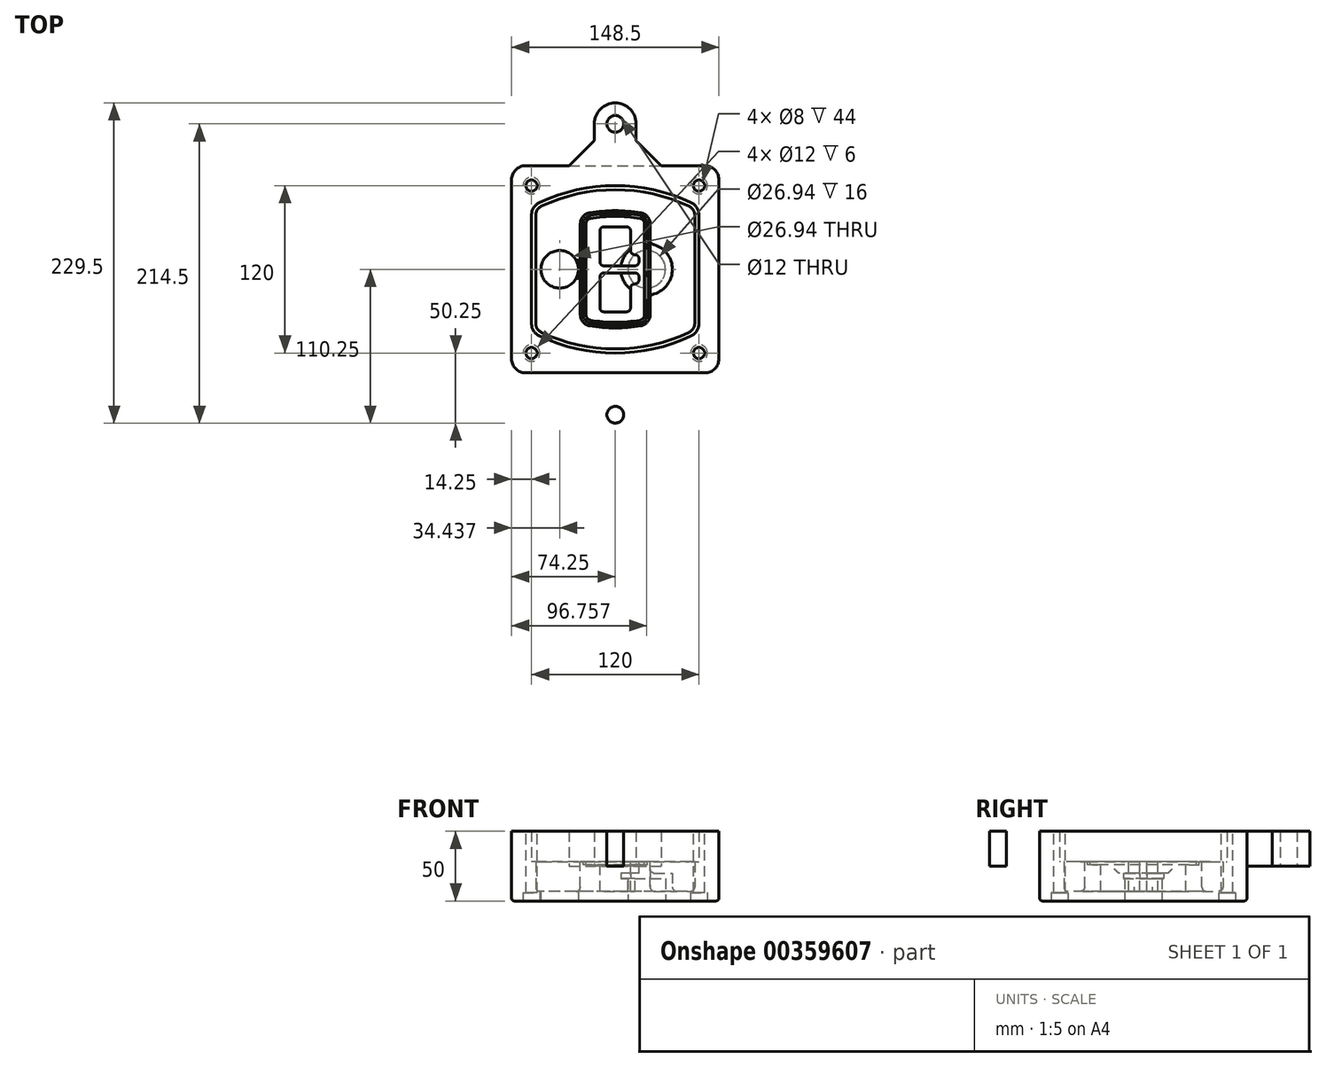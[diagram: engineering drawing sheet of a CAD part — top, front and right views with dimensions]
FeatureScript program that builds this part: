
annotation { "Feature Type Name" : "Feature", "Feature Type Description" : "" }
export const myFeature = defineFeature(function(context is Context, id is Id, definition is map)
    precondition{}
    {
        {
            var Q0;
            Q0=qCreatedBy(makeId("Top.planeOp"),FACE);
            var sketch = newSketch(context, id + "F0", { "sketchPlane" : qUnion([Q0])});
            skPoint(sketch, "E0.rect.middle", {"position": v(0, 0) * mm});
            skLineSegment(sketch, "E1.bottom", {"start": v(-64.25, -74.25) * mm, "end": v(64.25, -74.25) * mm});
            skLineSegment(sketch, "E1.top", {"start": v(-64.25, 74.25) * mm, "end": v(64.25, 74.25) * mm});
            skLineSegment(sketch, "E1.left", {"start": v(-74.25, -64.25) * mm, "end": v(-74.25, 64.25) * mm});
            skLineSegment(sketch, "E1.right", {"start": v(74.25, -64.25) * mm, "end": v(74.25, 64.25) * mm});
            skLineSegment(sketch, "E2", {"start": v(-74.25, 74.25) * mm, "end": v(74.25, -74.25) * mm, "construction": true});
            skLineSegment(sketch, "E3", {"start": v(74.25, 74.25) * mm, "end": v(-74.25, -74.25) * mm, "construction": true});
            skCircle(sketch, "E4", {"center": v(-60, 60) * mm, "radius": 4 * mm});
            skCircle(sketch, "E5", {"center": v(60, 60) * mm, "radius": 4 * mm});
            skCircle(sketch, "E6", {"center": v(60, -60) * mm, "radius": 4 * mm});
            skCircle(sketch, "E7", {"center": v(-60, -60) * mm, "radius": 4 * mm});
            skLineSegment(sketch, "E8", {"start": v(-60, 60) * mm, "end": v(60, 60) * mm, "construction": true});
            skLineSegment(sketch, "E9", {"start": v(60, 60) * mm, "end": v(60, -60) * mm, "construction": true});
            skLineSegment(sketch, "E10", {"start": v(60, -60) * mm, "end": v(-60, -60) * mm, "construction": true});
            skLineSegment(sketch, "E11", {"start": v(-60, -60) * mm, "end": v(-60, 60) * mm, "construction": true});
            skLineSegment(sketch, "E12", {"start": v(-60, 38.83) * mm, "end": v(-60, -38.83) * mm});
            skLineSegment(sketch, "E13", {"start": v(60, 38.83) * mm, "end": v(60, -38.83) * mm});
            skArc(sketch, "E14", {"start": v(54.26, 47.88) * mm, "mid": v(0, 60) * mm, "end": v(-54.26, 47.88) * mm});
            skArc(sketch, "E15", {"start": v(-54.26, -47.88) * mm, "mid": v(0, -60) * mm, "end": v(54.26, -47.88) * mm});
            skLineSegment(sketch, "E16", {"start": v(-60, 0) * mm, "end": v(60, 0) * mm, "construction": true});
            skPoint(sketch, "E17.visualSharp", {"position": v(-60, -45) * mm});
            skArc(sketch, "E17.filletArc", {"start": v(-60, -38.83) * mm, "mid": v(-58.44, -44.2) * mm, "end": v(-54.26, -47.88) * mm});
            skPoint(sketch, "E18.visualSharp", {"position": v(-60, 45) * mm});
            skArc(sketch, "E18.filletArc", {"start": v(-54.26, 47.88) * mm, "mid": v(-58.44, 44.2) * mm, "end": v(-60, 38.83) * mm});
            skPoint(sketch, "E19.visualSharp", {"position": v(60, 45) * mm});
            skArc(sketch, "E19.filletArc", {"start": v(60, 38.83) * mm, "mid": v(58.44, 44.2) * mm, "end": v(54.26, 47.88) * mm});
            skPoint(sketch, "E20.visualSharp", {"position": v(60, -45) * mm});
            skArc(sketch, "E20.filletArc", {"start": v(54.26, -47.88) * mm, "mid": v(58.44, -44.2) * mm, "end": v(60, -38.83) * mm});
            skPoint(sketch, "E21.visualSharp", {"position": v(-74.25, 74.25) * mm});
            skArc(sketch, "E21.filletArc", {"start": v(-64.25, 74.25) * mm, "mid": v(-71.32, 71.32) * mm, "end": v(-74.25, 64.25) * mm});
            skPoint(sketch, "E22.visualSharp", {"position": v(74.25, 74.25) * mm});
            skArc(sketch, "E22.filletArc", {"start": v(74.25, 64.25) * mm, "mid": v(71.32, 71.32) * mm, "end": v(64.25, 74.25) * mm});
            skPoint(sketch, "E23.visualSharp", {"position": v(74.25, -74.25) * mm});
            skArc(sketch, "E23.filletArc", {"start": v(64.25, -74.25) * mm, "mid": v(71.32, -71.32) * mm, "end": v(74.25, -64.25) * mm});
            skPoint(sketch, "E24.visualSharp", {"position": v(-74.25, -74.25) * mm});
            skArc(sketch, "E24.filletArc", {"start": v(-74.25, -64.25) * mm, "mid": v(-71.32, -71.32) * mm, "end": v(-64.25, -74.25) * mm});
            skArc(sketch, "E25.0", {"start": v(57, 38.83) * mm, "mid": v(55.9, 42.58) * mm, "end": v(52.98, 45.17) * mm});
            skLineSegment(sketch, "E25.1", {"start": v(57, 38.83) * mm, "end": v(57, -38.83) * mm});
            skArc(sketch, "E25.2", {"start": v(52.98, -45.17) * mm, "mid": v(55.9, -42.58) * mm, "end": v(57, -38.83) * mm});
            skArc(sketch, "E25.3", {"start": v(-52.98, -45.17) * mm, "mid": v(0, -57) * mm, "end": v(52.98, -45.17) * mm});
            skArc(sketch, "E25.4", {"start": v(-57, -38.83) * mm, "mid": v(-55.9, -42.58) * mm, "end": v(-52.98, -45.17) * mm});
            skArc(sketch, "E25.5", {"start": v(52.98, 45.17) * mm, "mid": v(0, 57) * mm, "end": v(-52.98, 45.17) * mm});
            skLineSegment(sketch, "E25.6", {"start": v(-57, 38.83) * mm, "end": v(-57, -38.83) * mm});
            skArc(sketch, "E25.7", {"start": v(-52.98, 45.17) * mm, "mid": v(-55.9, 42.58) * mm, "end": v(-57, 38.83) * mm});
            skArc(sketch, "E26.0", {"start": v(-55.96, 51.5) * mm, "mid": v(-61.82, 46.33) * mm, "end": v(-64, 38.83) * mm});
            skArc(sketch, "E26.1", {"start": v(55.96, 51.5) * mm, "mid": v(0, 64) * mm, "end": v(-55.96, 51.5) * mm});
            skArc(sketch, "E26.2", {"start": v(64, 38.83) * mm, "mid": v(61.82, 46.33) * mm, "end": v(55.96, 51.5) * mm});
            skLineSegment(sketch, "E26.3", {"start": v(64, 38.83) * mm, "end": v(64, -38.83) * mm});
            skArc(sketch, "E26.4", {"start": v(55.96, -51.5) * mm, "mid": v(61.82, -46.33) * mm, "end": v(64, -38.83) * mm});
            skLineSegment(sketch, "E26.5", {"start": v(-64, 38.83) * mm, "end": v(-64, -38.83) * mm});
            skArc(sketch, "E26.6", {"start": v(-55.96, -51.5) * mm, "mid": v(0, -64) * mm, "end": v(55.96, -51.5) * mm});
            skArc(sketch, "E26.7", {"start": v(-64, -38.83) * mm, "mid": v(-61.82, -46.33) * mm, "end": v(-55.96, -51.5) * mm});
            skSolve(sketch);
        }
        {
            var Q0;
            Q0=makeQuery(id+"F0.imprint","IMPRINT",FACE,{"disambiguationData":[TD([[makeQuery(id+"F0.imprint","IMPRINT",EDGE,{"derivedFrom":sQuery(id+"F0.wireOp",EDGE,"E1.bottom")}),1.0]])]});
            var Q1;
            Q1=makeQuery(id+"F0.imprint","IMPRINT",FACE,{"disambiguationData":[TD([[makeQuery(id+"F0.imprint","IMPRINT",EDGE,{"derivedFrom":sQuery(id+"F0.wireOp",EDGE,"E12")}),1.0]])]});
            var Q2;
            Q2=makeQuery(id+"F0.imprint","IMPRINT",FACE,{"disambiguationData":[TD([[makeQuery(id+"F0.imprint","IMPRINT",EDGE,{"derivedFrom":sQuery(id+"F0.wireOp",EDGE,"E25.0")}),1.0]])]});
            var Q3;
            Q3=makeQuery(id+"F0.imprint","IMPRINT",FACE,{"disambiguationData":[TD([[makeQuery(id+"F0.imprint","IMPRINT",EDGE,{"derivedFrom":sQuery(id+"F0.wireOp",EDGE,"E12")}),-1.0]])]});
            extrude(context, id + "F1", {"entities" : qUnion([Q0, Q1, Q2, Q3]), "oppositeDirection" : true, "depth" : 25 * mm});
        }
        {
            var Q0;
            Q0=makeQuery(id+"F0.imprint","IMPRINT",FACE,{"disambiguationData":[TD([[makeQuery(id+"F0.imprint","IMPRINT",EDGE,{"derivedFrom":sQuery(id+"F0.wireOp",EDGE,"E12")}),1.0]])]});
            extrude(context, id + "F2", {"entities" : qUnion([Q0]), "operationType" : NewBodyOperationType.ADD, "depth" : 3 * mm});
        }
        {
            var Q0;
            Q0=makeQuery(id+"F0.imprint","IMPRINT",FACE,{"disambiguationData":[TD([[makeQuery(id+"F0.imprint","IMPRINT",EDGE,{"derivedFrom":sQuery(id+"F0.wireOp",EDGE,"E25.0")}),1.0]])]});
            extrude(context, id + "F3", {"entities" : qUnion([Q0]), "operationType" : NewBodyOperationType.REMOVE, "oppositeDirection" : true, "depth" : 18 * mm});
        }
        {
            var Q0;
            Q0=makeQuery(id+"F2.opExtrude","CAP_FACE",FACE,{"disambiguationData":[OSD([sQuery(id+"F0.wireOp",EDGE,"E12"),sQuery(id+"F0.wireOp",EDGE,"E13"),sQuery(id+"F0.wireOp",EDGE,"E14"),sQuery(id+"F0.wireOp",EDGE,"E15"),sQuery(id+"F0.wireOp",EDGE,"E17.filletArc"),sQuery(id+"F0.wireOp",EDGE,"E18.filletArc"),sQuery(id+"F0.wireOp",EDGE,"E19.filletArc"),sQuery(id+"F0.wireOp",EDGE,"E20.filletArc"),sQuery(id+"F0.wireOp",EDGE,"E25.0"),sQuery(id+"F0.wireOp",EDGE,"E25.1"),sQuery(id+"F0.wireOp",EDGE,"E25.2"),sQuery(id+"F0.wireOp",EDGE,"E25.3"),sQuery(id+"F0.wireOp",EDGE,"E25.4"),sQuery(id+"F0.wireOp",EDGE,"E25.5"),sQuery(id+"F0.wireOp",EDGE,"E25.6"),sQuery(id+"F0.wireOp",EDGE,"E25.7")])],"isStart":false});
            var sketch = newSketch(context, id + "F4", { "sketchPlane" : qUnion([Q0])});
            skArc(sketch, "E27.0", {"start": v(-18.34, -40.45) * mm, "mid": v(0, -42) * mm, "end": v(18.34, -40.45) * mm});
            skArc(sketch, "E28.0", {"start": v(18.34, 40.45) * mm, "mid": v(0, 42) * mm, "end": v(-18.34, 40.45) * mm});
            skLineSegment(sketch, "E29", {"start": v(-25, 32.57) * mm, "end": v(-25, -32.57) * mm});
            skLineSegment(sketch, "E30", {"start": v(25, 32.57) * mm, "end": v(25, -32.57) * mm});
            skLineSegment(sketch, "E31", {"start": v(-25, 39.1) * mm, "end": v(25, 39.1) * mm, "construction": true});
            skLineSegment(sketch, "E32", {"start": v(-25, -39.1) * mm, "end": v(25, -39.1) * mm, "construction": true});
            skPoint(sketch, "E33.visualSharp", {"position": v(-25, 39.1) * mm});
            skArc(sketch, "E33.filletArc", {"start": v(-18.34, 40.45) * mm, "mid": v(-23.11, 37.73) * mm, "end": v(-25, 32.57) * mm});
            skPoint(sketch, "E34.visualSharp", {"position": v(25, 39.1) * mm});
            skArc(sketch, "E34.filletArc", {"start": v(25, 32.57) * mm, "mid": v(23.11, 37.73) * mm, "end": v(18.34, 40.45) * mm});
            skPoint(sketch, "E35.visualSharp", {"position": v(25, -39.1) * mm});
            skArc(sketch, "E35.filletArc", {"start": v(18.34, -40.45) * mm, "mid": v(23.11, -37.73) * mm, "end": v(25, -32.57) * mm});
            skPoint(sketch, "E36.visualSharp", {"position": v(-25, -39.1) * mm});
            skArc(sketch, "E36.filletArc", {"start": v(-25, -32.57) * mm, "mid": v(-23.11, -37.73) * mm, "end": v(-18.34, -40.45) * mm});
            skArc(sketch, "E37.0", {"start": v(52.98, 45.17) * mm, "mid": v(0, 57) * mm, "end": v(-52.98, 45.17) * mm});
            skArc(sketch, "E37.1", {"start": v(-52.98, 45.17) * mm, "mid": v(-55.9, 42.58) * mm, "end": v(-57, 38.83) * mm});
            skLineSegment(sketch, "E37.2", {"start": v(-57, 38.83) * mm, "end": v(-57, -38.83) * mm});
            skArc(sketch, "E37.3", {"start": v(-57, -38.83) * mm, "mid": v(-55.9, -42.58) * mm, "end": v(-52.98, -45.17) * mm});
            skArc(sketch, "E37.4", {"start": v(-52.98, -45.17) * mm, "mid": v(0, -57) * mm, "end": v(52.98, -45.17) * mm});
            skArc(sketch, "E37.5", {"start": v(52.98, -45.17) * mm, "mid": v(55.9, -42.58) * mm, "end": v(57, -38.83) * mm});
            skLineSegment(sketch, "E37.6", {"start": v(57, 38.83) * mm, "end": v(57, -38.83) * mm});
            skArc(sketch, "E37.7", {"start": v(57, 38.83) * mm, "mid": v(55.9, 42.58) * mm, "end": v(52.98, 45.17) * mm});
            skLineSegment(sketch, "E38.0", {"start": v(23, 32.57) * mm, "end": v(23, -32.57) * mm});
            skArc(sketch, "E38.1", {"start": v(18, -38.48) * mm, "mid": v(21.58, -36.44) * mm, "end": v(23, -32.57) * mm});
            skArc(sketch, "E38.2", {"start": v(-18, -38.48) * mm, "mid": v(0, -40) * mm, "end": v(18, -38.48) * mm});
            skArc(sketch, "E38.3", {"start": v(-23, -32.57) * mm, "mid": v(-21.58, -36.44) * mm, "end": v(-18, -38.48) * mm});
            skLineSegment(sketch, "E38.4", {"start": v(-23, 32.57) * mm, "end": v(-23, -32.57) * mm});
            skArc(sketch, "E38.5", {"start": v(23, 32.57) * mm, "mid": v(21.58, 36.44) * mm, "end": v(18, 38.48) * mm});
            skArc(sketch, "E38.6", {"start": v(-18, 38.48) * mm, "mid": v(-21.58, 36.44) * mm, "end": v(-23, 32.57) * mm});
            skArc(sketch, "E38.7", {"start": v(18, 38.48) * mm, "mid": v(0, 40) * mm, "end": v(-18, 38.48) * mm});
            skArc(sketch, "E39.0", {"start": v(21, 32.57) * mm, "mid": v(20.06, 35.15) * mm, "end": v(17.67, 36.5) * mm});
            skLineSegment(sketch, "E39.1", {"start": v(21, 32.57) * mm, "end": v(21, -32.57) * mm});
            skArc(sketch, "E39.2", {"start": v(17.67, -36.5) * mm, "mid": v(20.06, -35.15) * mm, "end": v(21, -32.57) * mm});
            skArc(sketch, "E39.3", {"start": v(-17.67, -36.5) * mm, "mid": v(0, -38) * mm, "end": v(17.67, -36.5) * mm});
            skArc(sketch, "E39.4", {"start": v(-21, -32.57) * mm, "mid": v(-20.06, -35.15) * mm, "end": v(-17.67, -36.5) * mm});
            skArc(sketch, "E39.5", {"start": v(17.67, 36.5) * mm, "mid": v(0, 38) * mm, "end": v(-17.67, 36.5) * mm});
            skLineSegment(sketch, "E39.6", {"start": v(-21, 32.57) * mm, "end": v(-21, -32.57) * mm});
            skArc(sketch, "E39.7", {"start": v(-17.67, 36.5) * mm, "mid": v(-20.06, 35.15) * mm, "end": v(-21, 32.57) * mm});
            skLineSegment(sketch, "E40", {"start": v(-25, 0) * mm, "end": v(25, 0) * mm, "construction": true});
            skLineSegment(sketch, "E41", {"start": v(-11, 5.5) * mm, "end": v(-11, 27.5) * mm});
            skLineSegment(sketch, "E42", {"start": v(-8, 30.5) * mm, "end": v(8, 30.5) * mm});
            skLineSegment(sketch, "E43", {"start": v(11, 27.5) * mm, "end": v(11, 13.5) * mm});
            skLineSegment(sketch, "E44", {"start": v(14, 10.5) * mm, "end": v(14, 10.5) * mm});
            skLineSegment(sketch, "E45", {"start": v(17, 7.5) * mm, "end": v(17, 5.5) * mm});
            skLineSegment(sketch, "E46", {"start": v(14, 2.5) * mm, "end": v(-8, 2.5) * mm});
            skPoint(sketch, "E47.visualSharp", {"position": v(-11, 30.5) * mm});
            skArc(sketch, "E47.filletArc", {"start": v(-8, 30.5) * mm, "mid": v(-10.12, 29.62) * mm, "end": v(-11, 27.5) * mm});
            skPoint(sketch, "E48.visualSharp", {"position": v(11, 30.5) * mm});
            skArc(sketch, "E48.filletArc", {"start": v(11, 27.5) * mm, "mid": v(10.12, 29.62) * mm, "end": v(8, 30.5) * mm});
            skPoint(sketch, "E49.visualSharp", {"position": v(11, 10.5) * mm});
            skArc(sketch, "E49.filletArc", {"start": v(11, 13.5) * mm, "mid": v(11.88, 11.38) * mm, "end": v(14, 10.5) * mm});
            skPoint(sketch, "E50.visualSharp", {"position": v(17, 10.5) * mm});
            skArc(sketch, "E50.filletArc", {"start": v(17, 7.5) * mm, "mid": v(16.12, 9.62) * mm, "end": v(14, 10.5) * mm});
            skPoint(sketch, "E51.visualSharp", {"position": v(17, 2.5) * mm});
            skArc(sketch, "E51.filletArc", {"start": v(14, 2.5) * mm, "mid": v(16.12, 3.38) * mm, "end": v(17, 5.5) * mm});
            skPoint(sketch, "E52.visualSharp", {"position": v(-11, 2.5) * mm});
            skArc(sketch, "E52.filletArc", {"start": v(-11, 5.5) * mm, "mid": v(-10.12, 3.38) * mm, "end": v(-8, 2.5) * mm});
            skLineSegment(sketch, "E53.0.MirrorCS", {"start": v(14, -2.5) * mm, "end": v(-8, -2.5) * mm});
            skArc(sketch, "E54.0.MirrorCS", {"start": v(-11, -5.5) * mm, "mid": v(-10.12, -3.38) * mm, "end": v(-8, -2.5) * mm});
            skLineSegment(sketch, "E55.0.MirrorCS", {"start": v(-11, -5.5) * mm, "end": v(-11, -27.5) * mm});
            skArc(sketch, "E56.0.MirrorCS", {"start": v(-8, -30.5) * mm, "mid": v(-10.12, -29.62) * mm, "end": v(-11, -27.5) * mm});
            skLineSegment(sketch, "E57.0.MirrorCS", {"start": v(-8, -30.5) * mm, "end": v(8, -30.5) * mm});
            skArc(sketch, "E58.0.MirrorCS", {"start": v(11, -27.5) * mm, "mid": v(10.12, -29.62) * mm, "end": v(8, -30.5) * mm});
            skLineSegment(sketch, "E59.0.MirrorCS", {"start": v(11, -27.5) * mm, "end": v(11, -13.5) * mm});
            skArc(sketch, "E60.0.MirrorCS", {"start": v(11, -13.5) * mm, "mid": v(11.88, -11.38) * mm, "end": v(14, -10.5) * mm});
            skArc(sketch, "E61.0.MirrorCS", {"start": v(17, -7.5) * mm, "mid": v(16.12, -9.62) * mm, "end": v(14, -10.5) * mm});
            skLineSegment(sketch, "E62.0.MirrorCS", {"start": v(17, -7.5) * mm, "end": v(17, -5.5) * mm});
            skArc(sketch, "E63.0.MirrorCS", {"start": v(14, -2.5) * mm, "mid": v(16.12, -3.38) * mm, "end": v(17, -5.5) * mm});
            skSolve(sketch);
        }
        {
            var Q0;
            Q0=makeQuery(id+"F4.imprint","IMPRINT",FACE,{"disambiguationData":[TD([[makeQuery(id+"F4.imprint","IMPRINT",EDGE,{"derivedFrom":sQuery(id+"F4.wireOp",EDGE,"E27.0")}),1.0]])]});
            var Q1;
            Q1=makeQuery(id+"F4.imprint","IMPRINT",FACE,{"disambiguationData":[TD([[makeQuery(id+"F4.imprint","IMPRINT",EDGE,{"derivedFrom":sQuery(id+"F4.wireOp",EDGE,"E38.0")}),-1.0]])]});
            var Q2;
            Q2=makeQuery(id+"F4.imprint","IMPRINT",FACE,{"disambiguationData":[TD([[makeQuery(id+"F4.imprint","IMPRINT",EDGE,{"derivedFrom":sQuery(id+"F4.wireOp",EDGE,"E39.0")}),1.0]])]});
            extrude(context, id + "F5", {"entities" : qUnion([Q0, Q1, Q2]), "operationType" : NewBodyOperationType.ADD, "endBound" : BoundingType.UP_TO_NEXT, "oppositeDirection" : true, "depth" : 25 * mm});
        }
        {
            var Q0;
            Q0=makeQuery(id+"F4.imprint","IMPRINT",FACE,{"disambiguationData":[TD([[makeQuery(id+"F4.imprint","IMPRINT",EDGE,{"derivedFrom":sQuery(id+"F4.wireOp",EDGE,"E38.0")}),-1.0]])]});
            extrude(context, id + "F6", {"entities" : qUnion([Q0]), "operationType" : NewBodyOperationType.REMOVE, "oppositeDirection" : true, "depth" : 2 * mm});
        }
        {
            var Q0;
            Q0=makeQuery(id+"F1.opExtrude","CAP_FACE",FACE,{"disambiguationData":[OSD([sQuery(id+"F0.wireOp",EDGE,"E1.bottom"),sQuery(id+"F0.wireOp",EDGE,"E1.top"),sQuery(id+"F0.wireOp",EDGE,"E1.left"),sQuery(id+"F0.wireOp",EDGE,"E1.right"),sQuery(id+"F0.wireOp",EDGE,"E4"),sQuery(id+"F0.wireOp",EDGE,"E5"),sQuery(id+"F0.wireOp",EDGE,"E6"),sQuery(id+"F0.wireOp",EDGE,"E7"),sQuery(id+"F0.wireOp",EDGE,"E21.filletArc"),sQuery(id+"F0.wireOp",EDGE,"E22.filletArc"),sQuery(id+"F0.wireOp",EDGE,"E23.filletArc"),sQuery(id+"F0.wireOp",EDGE,"E24.filletArc")])],"isStart":false});
            var sketch = newSketch(context, id + "F7", { "sketchPlane" : qUnion([Q0])});
            skCircle(sketch, "E64", {"center": v(22.5, 0) * mm, "radius": 13.47 * mm});
            skCircle(sketch, "E65", {"center": v(-39.81, 0) * mm, "radius": 13.47 * mm});
            skLineSegment(sketch, "E66", {"start": v(74.25, 0) * mm, "end": v(-74.25, 0) * mm});
            skCircle(sketch, "E67", {"center": v(22.5, 0) * mm, "radius": 18.47 * mm});
            skCircle(sketch, "E68", {"center": v(60, -60) * mm, "radius": 6 * mm});
            skCircle(sketch, "E69", {"center": v(-60, -60) * mm, "radius": 6 * mm});
            skCircle(sketch, "E70", {"center": v(-60, 60) * mm, "radius": 6 * mm});
            skCircle(sketch, "E71", {"center": v(60, 60) * mm, "radius": 6 * mm});
            skSolve(sketch);
        }
        {
            var Q0;
            {var subQ1=sQuery(id+"F7.wireOp",EDGE,"E66");var subQ4=sQuery(id+"F7.wireOp",EDGE,"E64");var subQ6=makeQuery(id+"F7.imprint","INTERSECT",VERTEX,{"disambiguationData":[OD(0.0)],"derivedFrom":[subQ4,subQ1]});Q0=makeQuery(id+"F7.imprint","IMPRINT",FACE,{"disambiguationData":[TD([[makeQuery(id+"F7.imprint","IMPRINT",EDGE,{"disambiguationData":[TD([[subQ6,-1.0]])],"derivedFrom":subQ4}),-1.0]])]});}
            var Q1;
            {var subQ0=sQuery(id+"F7.wireOp",EDGE,"E66");var subQ1=sQuery(id+"F7.wireOp",EDGE,"E64");var subQ3=makeQuery(id+"F7.imprint","INTERSECT",VERTEX,{"disambiguationData":[OD(0.0)],"derivedFrom":[subQ1,subQ0]});Q1=makeQuery(id+"F7.imprint","IMPRINT",FACE,{"disambiguationData":[TD([[makeQuery(id+"F7.imprint","IMPRINT",EDGE,{"disambiguationData":[TD([[subQ3,-1.0]])],"derivedFrom":subQ1}),1.0]])]});}
            var Q2;
            {var subQ0=sQuery(id+"F7.wireOp",EDGE,"E66");var subQ1=sQuery(id+"F7.wireOp",EDGE,"E64");var subQ3=makeQuery(id+"F7.imprint","INTERSECT",VERTEX,{"disambiguationData":[OD(0.0)],"derivedFrom":[subQ1,subQ0]});Q2=makeQuery(id+"F7.imprint","IMPRINT",FACE,{"disambiguationData":[TD([[makeQuery(id+"F7.imprint","IMPRINT",EDGE,{"disambiguationData":[TD([[subQ3,1.0]])],"derivedFrom":subQ1}),1.0]])]});}
            var Q3;
            {var subQ1=sQuery(id+"F7.wireOp",EDGE,"E66");var subQ4=sQuery(id+"F7.wireOp",EDGE,"E64");var subQ6=makeQuery(id+"F7.imprint","INTERSECT",VERTEX,{"disambiguationData":[OD(0.0)],"derivedFrom":[subQ4,subQ1]});Q3=makeQuery(id+"F7.imprint","IMPRINT",FACE,{"disambiguationData":[TD([[makeQuery(id+"F7.imprint","IMPRINT",EDGE,{"disambiguationData":[TD([[subQ6,1.0]])],"derivedFrom":subQ4}),-1.0]])]});}
            extrude(context, id + "F8", {"entities" : qUnion([Q0, Q1, Q2, Q3]), "operationType" : NewBodyOperationType.ADD, "oppositeDirection" : true, "depth" : 20 * mm});
        }
        {
            var Q0;
            {var subQ0=sQuery(id+"F7.wireOp",EDGE,"E66");var subQ1=sQuery(id+"F7.wireOp",EDGE,"E64");var subQ3=makeQuery(id+"F7.imprint","INTERSECT",VERTEX,{"disambiguationData":[OD(0.0)],"derivedFrom":[subQ1,subQ0]});Q0=makeQuery(id+"F7.imprint","IMPRINT",FACE,{"disambiguationData":[TD([[makeQuery(id+"F7.imprint","IMPRINT",EDGE,{"disambiguationData":[TD([[subQ3,-1.0]])],"derivedFrom":subQ1}),1.0]])]});}
            var Q1;
            {var subQ0=sQuery(id+"F7.wireOp",EDGE,"E66");var subQ1=sQuery(id+"F7.wireOp",EDGE,"E64");var subQ3=makeQuery(id+"F7.imprint","INTERSECT",VERTEX,{"disambiguationData":[OD(0.0)],"derivedFrom":[subQ1,subQ0]});Q1=makeQuery(id+"F7.imprint","IMPRINT",FACE,{"disambiguationData":[TD([[makeQuery(id+"F7.imprint","IMPRINT",EDGE,{"disambiguationData":[TD([[subQ3,1.0]])],"derivedFrom":subQ1}),1.0]])]});}
            extrude(context, id + "F9", {"entities" : qUnion([Q0, Q1]), "operationType" : NewBodyOperationType.REMOVE, "oppositeDirection" : true, "depth" : 16 * mm});
        }
        {
            var Q0;
            {var subQ0=sQuery(id+"F7.wireOp",EDGE,"E66");var subQ1=sQuery(id+"F7.wireOp",EDGE,"E65");var subQ3=makeQuery(id+"F7.imprint","INTERSECT",VERTEX,{"disambiguationData":[OD(0.0)],"derivedFrom":[subQ1,subQ0]});Q0=makeQuery(id+"F7.imprint","IMPRINT",FACE,{"disambiguationData":[TD([[makeQuery(id+"F7.imprint","IMPRINT",EDGE,{"disambiguationData":[TD([[subQ3,-1.0]])],"derivedFrom":subQ1}),1.0]])]});}
            var Q1;
            {var subQ0=sQuery(id+"F7.wireOp",EDGE,"E66");var subQ1=sQuery(id+"F7.wireOp",EDGE,"E65");var subQ3=makeQuery(id+"F7.imprint","INTERSECT",VERTEX,{"disambiguationData":[OD(0.0)],"derivedFrom":[subQ1,subQ0]});Q1=makeQuery(id+"F7.imprint","IMPRINT",FACE,{"disambiguationData":[TD([[makeQuery(id+"F7.imprint","IMPRINT",EDGE,{"disambiguationData":[TD([[subQ3,1.0]])],"derivedFrom":subQ1}),1.0]])]});}
            extrude(context, id + "F10", {"entities" : qUnion([Q0, Q1]), "operationType" : NewBodyOperationType.REMOVE, "oppositeDirection" : true, "depth" : 25 * mm});
        }
        {
            var Q0;
            Q0=makeQuery(id+"F7.imprint","IMPRINT",FACE,{"disambiguationData":[TD([[makeQuery(id+"F7.imprint","IMPRINT",EDGE,{"derivedFrom":sQuery(id+"F7.wireOp",EDGE,"E68")}),1.0]])]});
            var Q1;
            Q1=makeQuery(id+"F7.imprint","IMPRINT",FACE,{"disambiguationData":[TD([[makeQuery(id+"F7.imprint","IMPRINT",EDGE,{"derivedFrom":makeQuery(id+"F1.opExtrude","CAP_EDGE",EDGE,{"disambiguationData":[OSD([sQuery(id+"F0.wireOp",EDGE,"E5")])],"isStart":false})}),-1.0]])]});
            var Q2;
            Q2=makeQuery(id+"F7.imprint","IMPRINT",FACE,{"disambiguationData":[TD([[makeQuery(id+"F7.imprint","IMPRINT",EDGE,{"derivedFrom":sQuery(id+"F7.wireOp",EDGE,"E69")}),1.0]])]});
            var Q3;
            Q3=makeQuery(id+"F7.imprint","IMPRINT",FACE,{"disambiguationData":[TD([[makeQuery(id+"F7.imprint","IMPRINT",EDGE,{"derivedFrom":makeQuery(id+"F1.opExtrude","CAP_EDGE",EDGE,{"disambiguationData":[OSD([sQuery(id+"F0.wireOp",EDGE,"E4")])],"isStart":false})}),-1.0]])]});
            var Q4;
            Q4=makeQuery(id+"F7.imprint","IMPRINT",FACE,{"disambiguationData":[TD([[makeQuery(id+"F7.imprint","IMPRINT",EDGE,{"derivedFrom":sQuery(id+"F7.wireOp",EDGE,"E70")}),1.0]])]});
            var Q5;
            Q5=makeQuery(id+"F7.imprint","IMPRINT",FACE,{"disambiguationData":[TD([[makeQuery(id+"F7.imprint","IMPRINT",EDGE,{"derivedFrom":makeQuery(id+"F1.opExtrude","CAP_EDGE",EDGE,{"disambiguationData":[OSD([sQuery(id+"F0.wireOp",EDGE,"E7")])],"isStart":false})}),-1.0]])]});
            var Q6;
            Q6=makeQuery(id+"F7.imprint","IMPRINT",FACE,{"disambiguationData":[TD([[makeQuery(id+"F7.imprint","IMPRINT",EDGE,{"derivedFrom":sQuery(id+"F7.wireOp",EDGE,"E71")}),1.0]])]});
            var Q7;
            Q7=makeQuery(id+"F7.imprint","IMPRINT",FACE,{"disambiguationData":[TD([[makeQuery(id+"F7.imprint","IMPRINT",EDGE,{"derivedFrom":makeQuery(id+"F1.opExtrude","CAP_EDGE",EDGE,{"disambiguationData":[OSD([sQuery(id+"F0.wireOp",EDGE,"E6")])],"isStart":false})}),-1.0]])]});
            extrude(context, id + "F11", {"entities" : qUnion([Q0, Q1, Q2, Q3, Q4, Q5, Q6, Q7]), "operationType" : NewBodyOperationType.REMOVE, "oppositeDirection" : true, "depth" : 6 * mm});
        }
        {
            var Q0;
            Q0=makeQuery(id+"F9.boolean.opBoolean","COPY",FACE,{"derivedFrom":makeQuery(id+"F9.opExtrude","CAP_FACE",FACE,{"disambiguationData":[OSD([sQuery(id+"F7.wireOp",EDGE,"E64")])],"isStart":false})});
            var sketch = newSketch(context, id + "F12", { "sketchPlane" : qUnion([Q0])});
            skArc(sketch, "E72.0", {"start": v(11, 14.45) * mm, "mid": v(6.45, 9.13) * mm, "end": v(4.2, 2.5) * mm});
            skArc(sketch, "E72.1", {"start": v(4.2, -2.5) * mm, "mid": v(6.45, -9.13) * mm, "end": v(11, -14.45) * mm});
            skLineSegment(sketch, "E73", {"start": v(4.2, -2.5) * mm, "end": v(14, -2.5) * mm});
            skLineSegment(sketch, "E74.0", {"start": v(14, 2.5) * mm, "end": v(4.2, 2.5) * mm});
            skArc(sketch, "E74.1", {"start": v(14, 2.5) * mm, "mid": v(16.12, 3.38) * mm, "end": v(17, 5.5) * mm});
            skLineSegment(sketch, "E74.2", {"start": v(17, 7.5) * mm, "end": v(17, 5.5) * mm});
            skArc(sketch, "E74.3", {"start": v(17, 7.5) * mm, "mid": v(16.12, 9.62) * mm, "end": v(14, 10.5) * mm});
            skArc(sketch, "E74.4", {"start": v(11, 13.5) * mm, "mid": v(11.88, 11.38) * mm, "end": v(14, 10.5) * mm});
            skLineSegment(sketch, "E74.5", {"start": v(11, 14.45) * mm, "end": v(11, 13.5) * mm});
            skLineSegment(sketch, "E74.7", {"start": v(14, -2.5) * mm, "end": v(4.2, -2.5) * mm});
            skArc(sketch, "E74.8", {"start": v(14, -2.5) * mm, "mid": v(16.12, -3.38) * mm, "end": v(17, -5.5) * mm});
            skLineSegment(sketch, "E74.9", {"start": v(17, -7.5) * mm, "end": v(17, -5.5) * mm});
            skArc(sketch, "E74.10", {"start": v(17, -7.5) * mm, "mid": v(16.12, -9.62) * mm, "end": v(14, -10.5) * mm});
            skArc(sketch, "E74.11", {"start": v(11, -13.5) * mm, "mid": v(11.88, -11.38) * mm, "end": v(14, -10.5) * mm});
            skLineSegment(sketch, "E74.12", {"start": v(11, -14.45) * mm, "end": v(11, -13.5) * mm});
            skPoint(sketch, "E75.orphan", {"position": v(11, -27.5) * mm});
            skPoint(sketch, "E76.orphan", {"position": v(-8, -2.5) * mm});
            skPoint(sketch, "E77.orphan", {"position": v(-8, 2.5) * mm});
            skPoint(sketch, "E78.orphan", {"position": v(11, 27.5) * mm});
            skSolve(sketch);
        }
        {
            var Q0;
            {var subQ7=sQuery(id+"F12.wireOp",EDGE,"E72.0");var subQ14=sQuery(id+"F12.wireOp",EDGE,"E72.1");var subQ16=sQuery(id+"F12.wireOp",EDGE,"E74.1");var subQ18=sQuery(id+"F12.wireOp",EDGE,"E74.8");Q0=qUnion([makeQuery(id+"F12.imprint","IMPRINT",FACE,{"disambiguationData":[TD([[makeQuery(id+"F12.imprint","IMPRINT",EDGE,{"derivedFrom":subQ7}),1.0]])]}),makeQuery(id+"F12.imprint","IMPRINT",FACE,{"disambiguationData":[TD([[makeQuery(id+"F12.imprint","IMPRINT",EDGE,{"derivedFrom":subQ14}),1.0]])]}),makeQuery(id+"F12.imprint","IMPRINT",FACE,{"disambiguationData":[TD([[makeQuery(id+"F12.imprint","IMPRINT",EDGE,{"derivedFrom":subQ16}),1.0]])]}),makeQuery(id+"F12.imprint","IMPRINT",FACE,{"disambiguationData":[TD([[makeQuery(id+"F12.imprint","IMPRINT",EDGE,{"derivedFrom":subQ18}),-1.0]])]})]);}
            var Q1;
            Q1=makeQuery(id+"F5.boolean.opBoolean","SPLIT",FACE,{"disambiguationData":[TD([makeQuery(id+"F5.opExtrude","SWEPT_FACE",FACE,{"disambiguationData":[OSD([sQuery(id+"F4.wireOp",EDGE,"E41")])]})])],"derivedFrom":makeQuery(id+"F3.boolean.opBoolean","COPY",FACE,{"derivedFrom":makeQuery(id+"F3.opExtrude","CAP_FACE",FACE,{"disambiguationData":[OSD([sQuery(id+"F0.wireOp",EDGE,"E25.0"),sQuery(id+"F0.wireOp",EDGE,"E25.1"),sQuery(id+"F0.wireOp",EDGE,"E25.2"),sQuery(id+"F0.wireOp",EDGE,"E25.3"),sQuery(id+"F0.wireOp",EDGE,"E25.4"),sQuery(id+"F0.wireOp",EDGE,"E25.5"),sQuery(id+"F0.wireOp",EDGE,"E25.6"),sQuery(id+"F0.wireOp",EDGE,"E25.7")])],"isStart":false})})});
            extrude(context, id + "F13", {"entities" : qUnion([Q0]), "operationType" : NewBodyOperationType.REMOVE, "endBound" : BoundingType.UP_TO_SURFACE, "endBoundEntityFace" : qUnion([Q1]), "depth" : 25 * mm});
        }
        {
            var Q0;
            Q0=makeQuery(id+"F3.boolean.opBoolean","COPY",EDGE,{"derivedFrom":makeQuery(id+"F3.opExtrude","CAP_EDGE",EDGE,{"disambiguationData":[OSD([sQuery(id+"F0.wireOp",EDGE,"E25.6")])],"isStart":false})});
            var Q1;
            Q1=makeQuery(id+"F8.boolean.opBoolean","INTERSECT",EDGE,{"derivedFrom":[makeQuery(id+"F5.opExtrude","SWEPT_FACE",FACE,{"disambiguationData":[OSD([sQuery(id+"F4.wireOp",EDGE,"E30")])]}),makeQuery(id+"F8.opExtrude","CAP_FACE",FACE,{"disambiguationData":[OSD([sQuery(id+"F7.wireOp",EDGE,"E67")])],"isStart":false})]});
            var Q2;
            Q2=makeQuery(id+"F8.boolean.opBoolean","INTERSECT",EDGE,{"disambiguationData":[OD(1.0)],"derivedFrom":[makeQuery(id+"F5.opExtrude","SWEPT_FACE",FACE,{"disambiguationData":[OSD([sQuery(id+"F4.wireOp",EDGE,"E30")])]}),makeQuery(id+"F8.opExtrude","SWEPT_FACE",FACE,{"disambiguationData":[OSD([sQuery(id+"F7.wireOp",EDGE,"E67")])]})]});
            var Q3;
            {var subQ0=sQuery(id+"F4.wireOp",EDGE,"E30");Q3=makeQuery(id+"F8.boolean.opBoolean","SPLIT",EDGE,{"disambiguationData":[TD([makeQuery(id+"F5.opExtrude","SWEPT_FACE",FACE,{"disambiguationData":[OSD([sQuery(id+"F4.wireOp",EDGE,"E35.filletArc")])]})])],"derivedFrom":makeQuery(id+"F5.opExtrude","CAP_EDGE",EDGE,{"disambiguationData":[OSD([subQ0])],"isStart":false})});}
            var Q4;
            {var subQ0=sQuery(id+"F0.wireOp",EDGE,"E25.7");var subQ1=sQuery(id+"F0.wireOp",EDGE,"E25.1");var subQ2=sQuery(id+"F0.wireOp",EDGE,"E25.6");var subQ3=sQuery(id+"F0.wireOp",EDGE,"E25.5");var subQ4=sQuery(id+"F0.wireOp",EDGE,"E25.4");var subQ5=sQuery(id+"F0.wireOp",EDGE,"E25.0");var subQ6=sQuery(id+"F0.wireOp",EDGE,"E25.2");var subQ7=sQuery(id+"F0.wireOp",EDGE,"E25.3");Q4=makeQuery(id+"F8.boolean.opBoolean","INTERSECT",EDGE,{"derivedFrom":[makeQuery(id+"F5.boolean.opBoolean","SPLIT",FACE,{"disambiguationData":[TD([makeQuery(id+"F2.opExtrude","SWEPT_FACE",FACE,{"disambiguationData":[OSD([subQ5])]})])],"derivedFrom":makeQuery(id+"F3.boolean.opBoolean","COPY",FACE,{"derivedFrom":makeQuery(id+"F3.opExtrude","CAP_FACE",FACE,{"disambiguationData":[OSD([subQ5,subQ1,subQ6,subQ7,subQ4,subQ3,subQ2,subQ0])],"isStart":false})})}),makeQuery(id+"F8.opExtrude","SWEPT_FACE",FACE,{"disambiguationData":[OSD([sQuery(id+"F7.wireOp",EDGE,"E67")])]})]});}
            var Q5;
            Q5=makeQuery(id+"F8.boolean.opBoolean","INTERSECT",EDGE,{"disambiguationData":[OD(0.0)],"derivedFrom":[makeQuery(id+"F5.opExtrude","SWEPT_FACE",FACE,{"disambiguationData":[OSD([sQuery(id+"F4.wireOp",EDGE,"E30")])]}),makeQuery(id+"F8.opExtrude","SWEPT_FACE",FACE,{"disambiguationData":[OSD([sQuery(id+"F7.wireOp",EDGE,"E67")])]})]});
            fillet(context, id + "F14", {"entities" : qUnion([Q0, Q1, Q2, Q3, Q4, Q5]), "radius" : 3 * mm, "tangentPropagation" : true, "allowEdgeOverflow" : false});
        }
        {
            var Q0;
            Q0=makeQuery(id+"F1.opExtrude","CAP_EDGE",EDGE,{"disambiguationData":[OSD([sQuery(id+"F0.wireOp",EDGE,"E1.bottom")])],"isStart":false});
            fillet(context, id + "F15", {"entities" : qUnion([Q0]), "radius" : 2 * mm, "tangentPropagation" : true, "allowEdgeOverflow" : false});
        }
        {
            var Q0;
            {var subQ0=sQuery(id+"F0.wireOp",EDGE,"E21.filletArc");var subQ1=sQuery(id+"F0.wireOp",EDGE,"E7");var subQ2=sQuery(id+"F0.wireOp",EDGE,"E6");var subQ3=sQuery(id+"F0.wireOp",EDGE,"E5");var subQ4=sQuery(id+"F0.wireOp",EDGE,"E4");var subQ5=sQuery(id+"F0.wireOp",EDGE,"E22.filletArc");var subQ6=sQuery(id+"F0.wireOp",EDGE,"E1.bottom");var subQ7=sQuery(id+"F0.wireOp",EDGE,"E1.right");var subQ8=sQuery(id+"F0.wireOp",EDGE,"E1.top");var subQ9=sQuery(id+"F0.wireOp",EDGE,"E1.left");var subQ10=sQuery(id+"F0.wireOp",EDGE,"E23.filletArc");var subQ11=sQuery(id+"F0.wireOp",EDGE,"E24.filletArc");Q0=makeQuery(id+"F2.boolean.opBoolean","SPLIT",FACE,{"disambiguationData":[TD([makeQuery(id+"F1.opExtrude","SWEPT_FACE",FACE,{"disambiguationData":[OSD([subQ6])]})])],"derivedFrom":makeQuery(id+"F1.opExtrude","CAP_FACE",FACE,{"disambiguationData":[OSD([subQ6,subQ8,subQ9,subQ7,subQ4,subQ3,subQ2,subQ1,subQ0,subQ5,subQ10,subQ11])],"isStart":true})});}
            var sketch = newSketch(context, id + "F16", { "sketchPlane" : qUnion([Q0])});
            skLineSegment(sketch, "E79", {"start": v(-15, 92.25) * mm, "end": v(-15, 104.25) * mm});
            skArc(sketch, "E80", {"start": v(15, 104.25) * mm, "mid": v(0, 119.25) * mm, "end": v(-15, 104.25) * mm});
            skLineSegment(sketch, "E81", {"start": v(0, 104.25) * mm, "end": v(0, 74.25) * mm, "construction": true});
            skCircle(sketch, "E82", {"center": v(0, 104.25) * mm, "radius": 6 * mm});
            skLineSegment(sketch, "E83", {"start": v(-33, 74.25) * mm, "end": v(-15, 92.25) * mm});
            skLineSegment(sketch, "E84", {"start": v(15, 104.25) * mm, "end": v(15, 92.25) * mm});
            skLineSegment(sketch, "E85", {"start": v(15, 92.25) * mm, "end": v(33, 74.25) * mm});
            skLineSegment(sketch, "E86", {"start": v(-74.25, 0) * mm, "end": v(74.25, 0) * mm, "construction": true});
            skLineSegment(sketch, "E87.MirrorCS", {"start": v(0, -104.25) * mm, "end": v(0, -74.25) * mm, "construction": true});
            skCircle(sketch, "E88.MirrorC", {"center": v(0, -104.25) * mm, "radius": 6 * mm});
            skLineSegment(sketch, "E89.MirrorCS", {"start": v(15, -104.25) * mm, "end": v(15, -92.25) * mm});
            skArc(sketch, "E90.MirrorCS", {"start": v(15, -104.25) * mm, "mid": v(0, -119.25) * mm, "end": v(-15, -104.25) * mm});
            skLineSegment(sketch, "E91.MirrorCS", {"start": v(-33, -74.25) * mm, "end": v(-15, -92.25) * mm});
            skLineSegment(sketch, "E92.MirrorCS", {"start": v(15, -92.25) * mm, "end": v(33, -74.25) * mm});
            skLineSegment(sketch, "E93.MirrorCS", {"start": v(-15, -92.25) * mm, "end": v(-15, -104.25) * mm});
            skSolve(sketch);
        }
        {
            var Q0;
            Q0=makeQuery(id+"F16.imprint","IMPRINT",FACE,{"disambiguationData":[TD([[makeQuery(id+"F16.imprint","IMPRINT",EDGE,{"derivedFrom":makeQuery(id+"F1.opExtrude","CAP_EDGE",EDGE,{"disambiguationData":[OSD([sQuery(id+"F0.wireOp",EDGE,"E1.bottom")])],"isStart":true})}),1.0]])]});
            var Q1;
            Q1=makeQuery(id+"F16.imprint","IMPRINT",FACE,{"disambiguationData":[TD([[makeQuery(id+"F16.imprint","IMPRINT",EDGE,{"derivedFrom":sQuery(id+"F16.wireOp",EDGE,"E79")}),-1.0]])]});
            extrude(context, id + "F17", {"entities" : qUnion([Q0, Q1]), "operationType" : NewBodyOperationType.ADD, "depth" : 25 * mm});
        }
        {
            var Q0;
            Q0=makeQuery(id+"F16.imprint","IMPRINT",FACE,{"disambiguationData":[TD([[makeQuery(id+"F16.imprint","IMPRINT",EDGE,{"derivedFrom":sQuery(id+"F16.wireOp",EDGE,"E88.MirrorC")}),1.0]])]});
            extrude(context, id + "F18", {"entities" : qUnion([Q0]), "operationType" : NewBodyOperationType.ADD, "depth" : 25 * mm});
        }
    });
